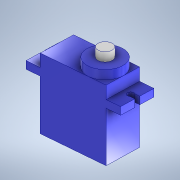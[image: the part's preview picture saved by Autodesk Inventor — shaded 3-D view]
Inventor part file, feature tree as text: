
AUTODESK INVENTOR PART (.ipt)
format: ipt  version: 2022 (Build 260153000, 153)  size: 164,864 bytes
history: native  units: mm
features: extrude x4, sketch x3, other x2
ambient origin geometry x8: Origin, YZ Plane, XZ Plane, XY Plane, X Axis, Y Axis, Z Axis, Center Point
bodies: Body1 (feature_tree)
feature tree (9):
  other  "ソリッド1"
  sketch  "スケッチ1"
  extrude  "軸台"  Depth=8.7mm
  extrude  "本体"  Depth=27.7mm
  other  "作業平面1"
  extrude  "タブ"  Depth=3.0mm TaperAngle=0.0deg
  extrude  "軸"  TaperAngle=0.0deg  [1 undecoded]
  sketch  "スケッチ2"
  sketch  "スケッチ3"
note: 1 required parameter value undecoded (feature->parameter linkage not recoverable at this tier; creation-order binding heuristic only, values carry confidence <= 0.55)
